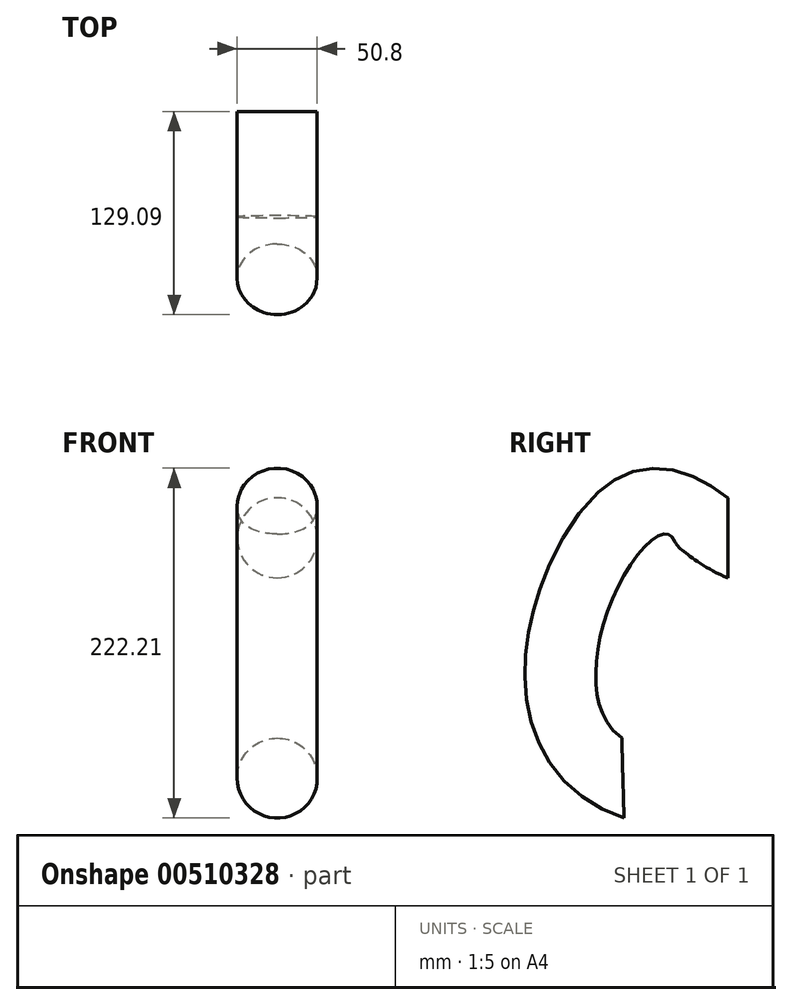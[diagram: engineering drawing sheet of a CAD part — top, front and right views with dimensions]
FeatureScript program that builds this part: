
annotation { "Feature Type Name" : "Feature", "Feature Type Description" : "" }
export const myFeature = defineFeature(function(context is Context, id is Id, definition is map)
    precondition{}
    {
        {
            var Q0;
            Q0=qCreatedBy(makeId("Front.planeOp"),FACE);
            var sketch = newSketch(context, id + "F0", { "sketchPlane" : qUnion([Q0])});
            skCircle(sketch, "E0", {"center": v(0, 0) * mm, "radius": 25.4 * mm});
            skSolve(sketch);
        }
        {
            var Q0;
            Q0=qCreatedBy(makeId("Right.planeOp"),FACE);
            var sketch = newSketch(context, id + "F1", { "sketchPlane" : qUnion([Q0])});
            skFitSpline(sketch, "E1", {"points": [v(0, 0) * mm, v(-60.87, 15.73) * mm, v(-66.87, -152.58) * mm], "startDerivative": vector(-149.4, 74.9) * mm, "endDerivative": vector(344.68, -161.6) * mm});
            skSolve(sketch);
        }
        {
            var Q0;
            Q0=makeQuery(id+"F0.imprint","IMPRINT",FACE,{"disambiguationData":[TD([[makeQuery(id+"F0.imprint","IMPRINT",EDGE,{"derivedFrom":sQuery(id+"F0.wireOp",EDGE,"E0")}),1.0]])]});
            var Q1;
            Q1=sQuery(id+"F1.wireOp",EDGE,"E1");
            sweep(context, id + "F2", {"profiles" : qUnion([Q0]), "path" : qUnion([Q1])});
        }
    });
